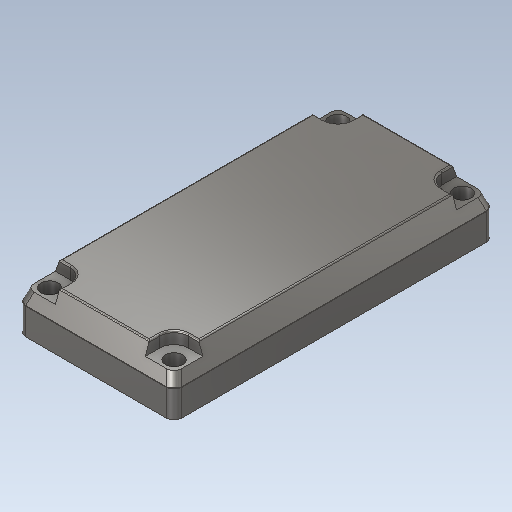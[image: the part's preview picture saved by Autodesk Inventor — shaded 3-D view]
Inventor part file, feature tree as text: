
AUTODESK INVENTOR PART (.ipt)
format: ipt  version: 2020 (Build 240168000, 168)  size: 270,848 bytes
history: native  units: mm
features: other x4, mirror x4, chamfer x4, extrude x3, fillet x2, sketch x2
ambient origin geometry x8: Origin, YZ Plane, XZ Plane, XY Plane, X Axis, Y Axis, Z Axis, Center Point
bodies: Body1 (feature_tree)
feature tree (19):
  other  "Sólido1"
  extrude  "Extrusión1"  Depth=40.6mm
  extrude  "Extrusión2"  Depth=0.2mm
  mirror  "Simetría1"
  mirror  "Simetría2"
  extrude  "Extrusión3"  Depth=0.2mm TaperAngle=0.0deg
  mirror  "Simetría3"
  mirror  "Simetría4"
  chamfer  "Chaflán1"  Distance=2.2mm
  chamfer  "Chaflán2"  Distance=2.2mm
  chamfer  "Chaflán3"  Distance=2.2mm
  chamfer  "Chaflán4"  Distance=1.5mm
  fillet  "Empalme1"  Radius=2.0mm
  fillet  "Empalme2"  Radius=2.0mm
  sketch  "Boceto1"  dims[d0=19.8mm d1=40.6mm]
  other  "Eje de trabajo1"
  other  "Eje de trabajo2"
  other  "Eje de trabajo3"
  sketch  "Boceto4"  dims[d2=6.4mm d3=0.0mm d6=3.6mm d8=1.5mm d9=0.0mm d10=2.2mm d11=2.2mm d12=2.2mm d13=1.5mm d14=0.0mm d15=3.0mm d16=2.0mm d17=3.490659mm d18=3.0mm d19=2.0mm d20=3.490659mm d21=3.0mm d22=2.0mm d23=3.490659mm d24=3.0mm d25=2.0mm d26=3.490659mm d27=1.0mm d28=0.2mm]
